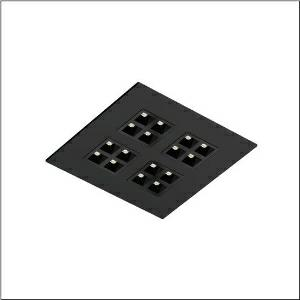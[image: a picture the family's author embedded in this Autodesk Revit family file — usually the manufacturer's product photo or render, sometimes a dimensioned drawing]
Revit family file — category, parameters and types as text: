
# Revit family: silica_31_square_51my6ldu44ba
name_source: partatom
category: Lighting Fixtures
units: mm (PartAtom-declared; Revit-internal decimal feet)

## family parameters
Cut with Voids When Loaded = No
Host = Face
Light Source = No
Part Type = Normal
Room Calculation Point = No
Round Connector Dimension = Use Diameter
Shared = No

## types (1)
- --- (1 x LED, 6310 lm, 38.5 W, 4000K)
    Apparent Load = 39 VA
    CIE Flux Codes = 82 100 100 100 100
    Color Rendering = 80
    Color Temperature = 4000K
    Default Elevation = 1800 mm
    Description = Silica 31 Square, office luminaire, primary light control with lens, of PMMA, primary anti-glare with reflector, of PC, black, light emission: direct distribution, primary light characteristic: symmetric, installation type: lay-in mounting, LED, rated luminous flux: 4.620lm, luminous efficacy: 167lm/W, light colour: 840, colour temperature: 4000K, control gear: DALI 2, Multilumen, with terminal, 5-pole, mains connection: 220..240V, AC, 50/60Hz, rated input power: 27.6W, luminaire housing, of sheet steel, coated, jet black (RAL 9005), module: M625, length: 620mm, width: 620mm, height: 43mm, protection rating (complete): IP20, insulation class (complete): insulation class II (safety insulation), certification: CE, impact resistance: IK03, permissible operating ambient temperature: -20..+35°C, standard: EN 50419, packaging unit: 1 piece
    Height = 0 mm  [stored 0 ft]
    Lamp = 1 x LED
    Lamp Light Flux = 6310 lm
    Lamp Power = 38.5 W
    Lamp count = 1
    Length = 620 mm
    Luminous efficacy = 164 lm/W
    Manufacturer = Siteco
    ModVariant = No
    Model = 51MY6LDU44BA
    Mounting Place = Ceiling
    Mounting Type = Recessed
    Number of Poles = 1
    OnlyDefault = Yes
    Power Factor = 1
    Product Name = Silica 31 Square
    Product group = office luminaire | ceiling recessed
    ProductGroupID = 400
    Protection Class = Protection class II
    Protection Degree = IP 20
    RLX_Detail_Level = 1
    RLX_Emergency_Light_Flux = 0 lm
    RLX_Emergency_Type = 0
    RLX_Emergency_Type_DB = No
    RlxData = <blob elided: 35485 chars, md5=ccc14198>
    Socket = socket
    Standby Power = 0 W
    System Light Flux = 6310 lm
    System Power = 39 W
    Type Comments = factory setting: luminous flux: 100 % | (OFF | OFF | OFF | OFF) | 1050 mA
    Type Image = l_1313660.jpg
    URL = http://relux.com
    VarID = @adj_043321
    Voltage = 0 V
    Weight = 0.00 kg
    Width = 620 mm

note: [stored X ft] marks values corroborated as IEEE doubles in the binary element streams (Revit-internal decimal feet)

## geometry (parser evidence)
native form markers: Blend x4, Sweep x11
no freeform markers — native parametric forms only
